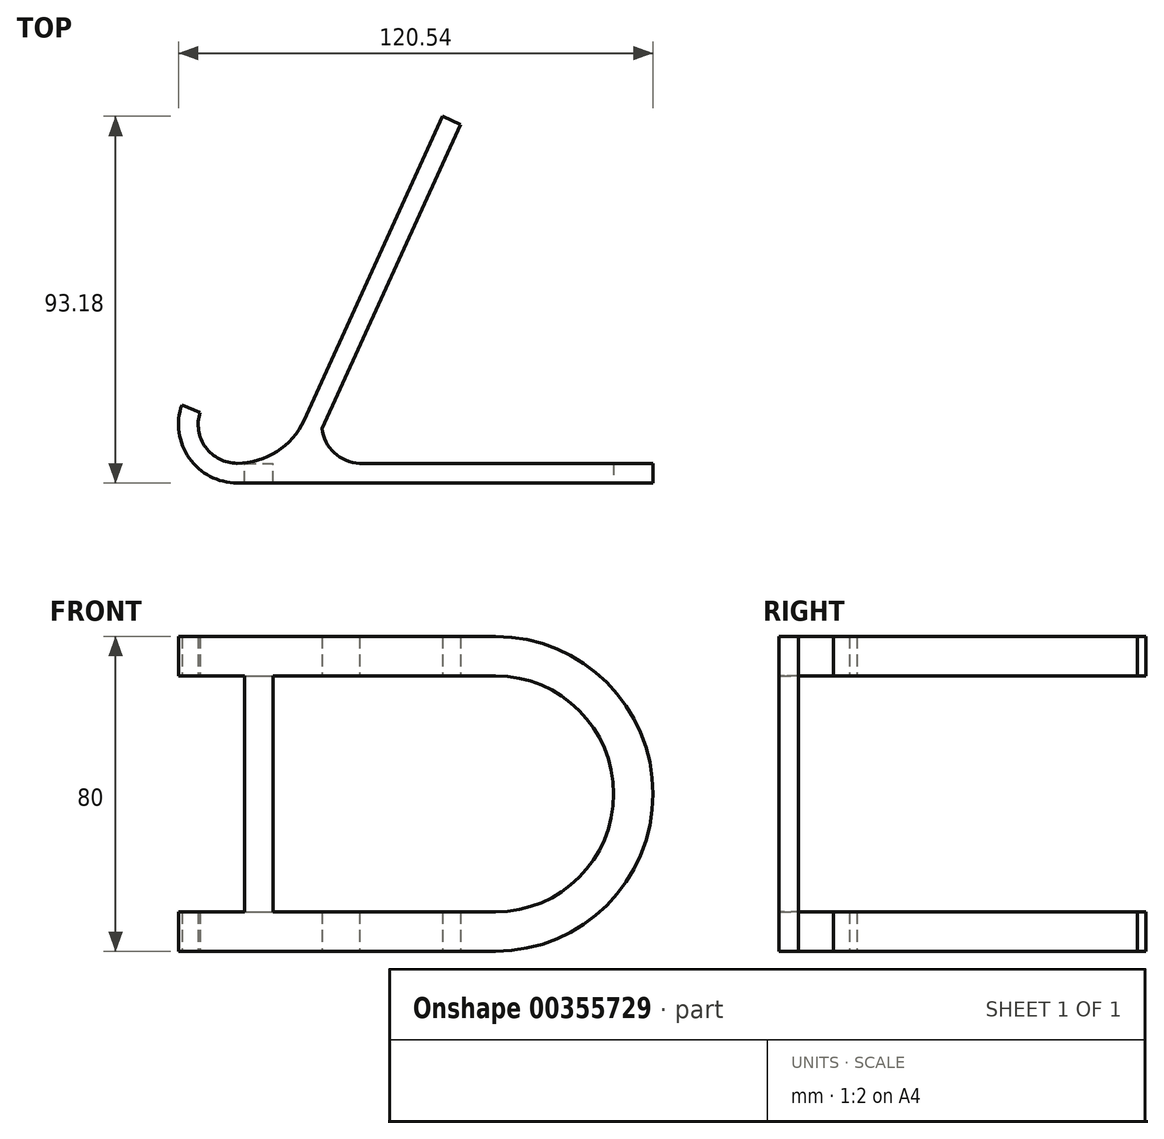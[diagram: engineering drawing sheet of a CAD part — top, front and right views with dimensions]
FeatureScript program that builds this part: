
annotation { "Feature Type Name" : "Feature", "Feature Type Description" : "" }
export const myFeature = defineFeature(function(context is Context, id is Id, definition is map)
    precondition{}
    {
        {
            var Q0;
            Q0=qCreatedBy(makeId("Top.planeOp"),FACE);
            var sketch = newSketch(context, id + "F0", { "sketchPlane" : qUnion([Q0])});
            skLineSegment(sketch, "E0", {"start": v(0, 0) * mm, "end": v(-65.65, 0) * mm});
            skArc(sketch, "E1", {"start": v(-79.68, 19.85) * mm, "mid": v(-77.8, 6.3) * mm, "end": v(-65.65, 0) * mm});
            skArc(sketch, "E2.0", {"start": v(-75.05, 17.94) * mm, "mid": v(-73.65, 9.07) * mm, "end": v(-65.65, 5) * mm});
            skLineSegment(sketch, "E2.1", {"start": v(0, 5) * mm, "end": v(-65.65, 5) * mm});
            skLineSegment(sketch, "E3", {"start": v(-79.68, 19.85) * mm, "end": v(-75.05, 17.94) * mm});
            skLineSegment(sketch, "E4", {"start": v(0, 5) * mm, "end": v(0, 0) * mm});
            skArc(sketch, "E5", {"start": v(-65.65, 5) * mm, "mid": v(-55.55, 7.97) * mm, "end": v(-48.67, 15.92) * mm});
            skLineSegment(sketch, "E6", {"start": v(-48.67, 15.92) * mm, "end": v(-13.43, 93.18) * mm});
            skLineSegment(sketch, "E7", {"start": v(-13.43, 93.18) * mm, "end": v(-8.88, 91.1) * mm});
            skLineSegment(sketch, "E8", {"start": v(-8.88, 91.1) * mm, "end": v(-48.15, 5) * mm});
            skArc(sketch, "E9", {"start": v(-44.11, 13.86) * mm, "mid": v(-40.65, 7.39) * mm, "end": v(-33.71, 5) * mm});
            skSolve(sketch);
        }
        {
            var Q0;
            Q0 = qSketchRegion(id + "F0", true);
            extrude(context, id + "F1", {"entities" : qUnion([Q0]), "depth" : 10 * mm});
        }
        {
            var Q0;
            Q0=makeQuery(id+"F1.opExtrude","CAP_FACE",FACE,{"disambiguationData":[OSD([sQuery(id+"F0.wireOp",EDGE,"E0"),sQuery(id+"F0.wireOp",EDGE,"E1"),sQuery(id+"F0.wireOp",EDGE,"E2.0"),sQuery(id+"F0.wireOp",EDGE,"E2.1"),sQuery(id+"F0.wireOp",EDGE,"E3"),sQuery(id+"F0.wireOp",EDGE,"E4"),sQuery(id+"F0.wireOp",EDGE,"E5"),sQuery(id+"F0.wireOp",EDGE,"E6"),sQuery(id+"F0.wireOp",EDGE,"E7"),sQuery(id+"F0.wireOp",EDGE,"E8"),sQuery(id+"F0.wireOp",EDGE,"E9")])],"isStart":false});
            extrude(context, id + "F2", {"entities" : qUnion([Q0]), "depth" : 70 * mm, "hasSecondDirection" : true, "secondDirectionOppositeDirection" : true, "secondDirectionDepth" : -60 * mm});
        }
        {
            var Q0;
            Q0=qCreatedBy(makeId("Front.planeOp"),FACE);
            var sketch = newSketch(context, id + "F3", { "sketchPlane" : qUnion([Q0])});
            skLineSegment(sketch, "E10", {"start": v(-63.77, 6.96) * mm, "end": v(-63.77, 73.26) * mm});
            skLineSegment(sketch, "E11", {"start": v(-56.46, 6.4) * mm, "end": v(-56.46, 73.87) * mm});
            skLineSegment(sketch, "E12", {"start": v(-63.77, 73.26) * mm, "end": v(-56.46, 73.87) * mm});
            skLineSegment(sketch, "E13", {"start": v(-63.77, 6.96) * mm, "end": v(-56.46, 6.4) * mm});
            skArc(sketch, "E14", {"start": v(0, 0) * mm, "mid": v(40, 40) * mm, "end": v(0, 80) * mm});
            skArc(sketch, "E15.0", {"start": v(0, 10) * mm, "mid": v(30, 40) * mm, "end": v(0, 70) * mm});
            skLineSegment(sketch, "E16", {"start": v(0, 80) * mm, "end": v(0, 70) * mm});
            skLineSegment(sketch, "E17", {"start": v(0, 10) * mm, "end": v(0, 0) * mm});
            skSolve(sketch);
        }
        {
            var Q0;
            Q0 = qSketchRegion(id + "F3", true);
            extrude(context, id + "F4", {"entities" : qUnion([Q0]), "operationType" : NewBodyOperationType.ADD, "oppositeDirection" : true, "depth" : 5 * mm});
        }
    });
